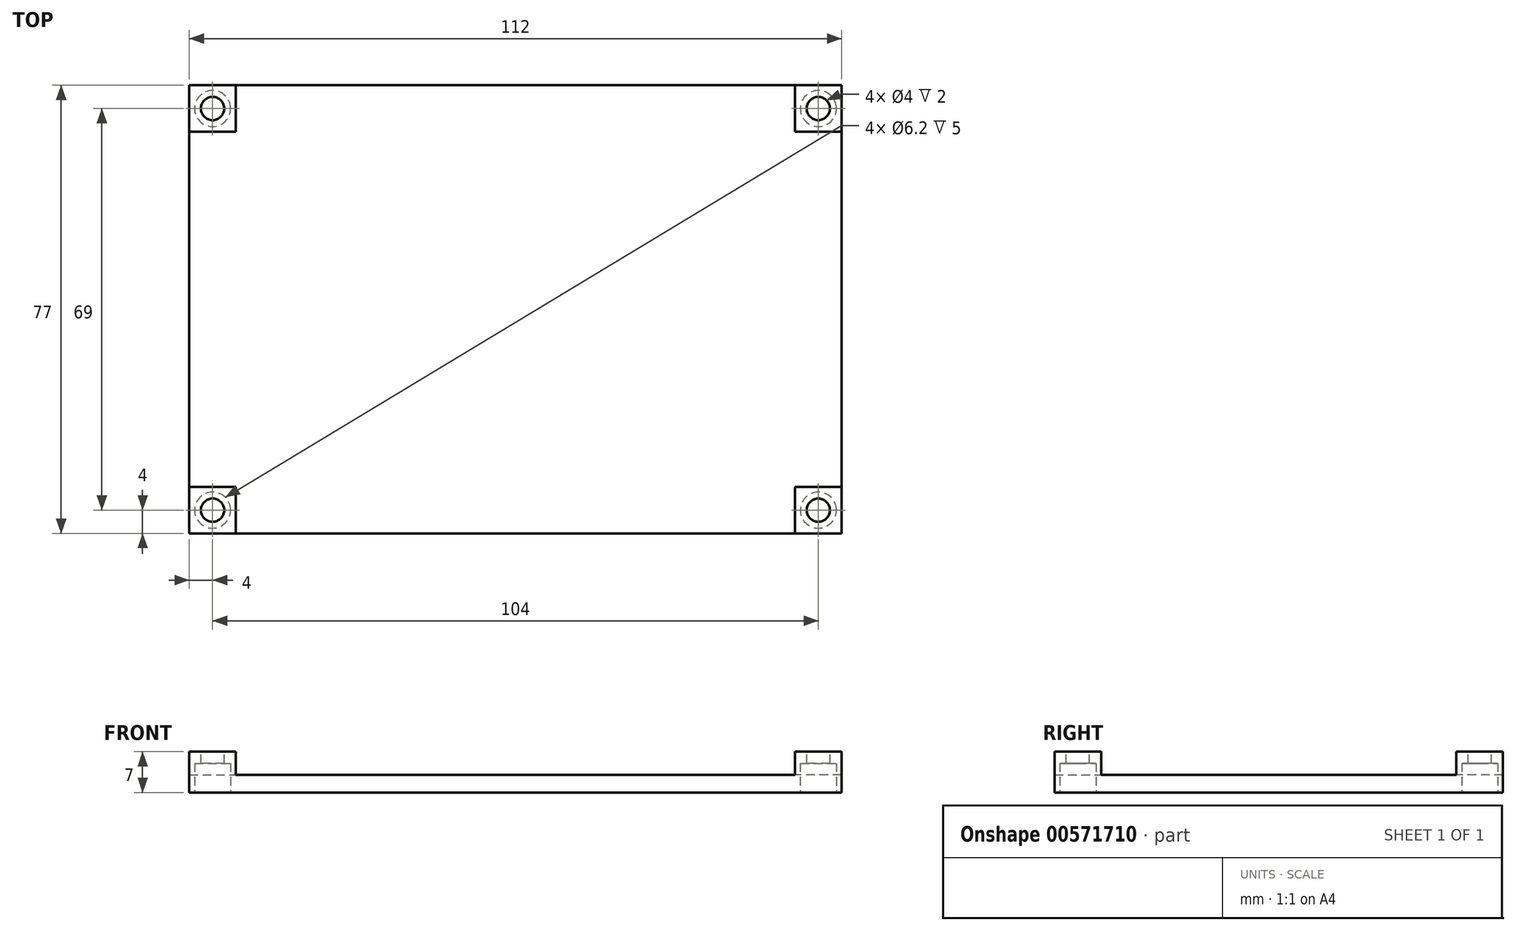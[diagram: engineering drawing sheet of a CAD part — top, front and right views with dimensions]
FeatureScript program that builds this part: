
annotation { "Feature Type Name" : "Feature", "Feature Type Description" : "" }
export const myFeature = defineFeature(function(context is Context, id is Id, definition is map)
    precondition{}
    {
        {
            var Q0;
            Q0=qCreatedBy(makeId("Top.planeOp"),FACE);
            var sketch = newSketch(context, id + "F0", { "sketchPlane" : qUnion([Q0])});
            skLineSegment(sketch, "E0.bottom", {"start": v(56, -38.5) * mm, "end": v(-56, -38.5) * mm});
            skLineSegment(sketch, "E0.top", {"start": v(56, 38.5) * mm, "end": v(-56, 38.5) * mm});
            skLineSegment(sketch, "E0.left", {"start": v(56, -38.5) * mm, "end": v(56, 38.5) * mm});
            skLineSegment(sketch, "E0.right", {"start": v(-56, -38.5) * mm, "end": v(-56, 38.5) * mm});
            skPoint(sketch, "E0.middle", {"position": v(0, 0) * mm});
            skSolve(sketch);
        }
        {
            var Q0;
            Q0=makeQuery(id+"F0.imprint","IMPRINT",FACE,{"disambiguationData":[TD([[makeQuery(id+"F0.imprint","IMPRINT",EDGE,{"derivedFrom":sQuery(id+"F0.wireOp",EDGE,"E0.bottom")}),-1.0]])]});
            extrude(context, id + "F1", {"entities" : qUnion([Q0]), "depth" : 3 * mm, "offsetDistance" : 25.4 * mm});
        }
        {
            var Q0;
            Q0=makeQuery(id+"F1.opExtrude","CAP_FACE",FACE,{"disambiguationData":[OSD([sQuery(id+"F0.wireOp",EDGE,"E0.bottom"),sQuery(id+"F0.wireOp",EDGE,"E0.top"),sQuery(id+"F0.wireOp",EDGE,"E0.left"),sQuery(id+"F0.wireOp",EDGE,"E0.right")])],"isStart":false});
            var sketch = newSketch(context, id + "F2", { "sketchPlane" : qUnion([Q0])});
            skLineSegment(sketch, "E1.bottom", {"start": v(-56, 38.5) * mm, "end": v(-48, 38.5) * mm});
            skLineSegment(sketch, "E1.top", {"start": v(-56, 30.5) * mm, "end": v(-48, 30.5) * mm});
            skLineSegment(sketch, "E1.left", {"start": v(-56, 38.5) * mm, "end": v(-56, 30.5) * mm});
            skLineSegment(sketch, "E1.right", {"start": v(-48, 38.5) * mm, "end": v(-48, 30.5) * mm});
            skLineSegment(sketch, "E2.bottom", {"start": v(56, 38.5) * mm, "end": v(48, 38.5) * mm});
            skLineSegment(sketch, "E2.top", {"start": v(56, 30.5) * mm, "end": v(48, 30.5) * mm});
            skLineSegment(sketch, "E2.left", {"start": v(56, 38.5) * mm, "end": v(56, 30.5) * mm});
            skLineSegment(sketch, "E2.right", {"start": v(48, 38.5) * mm, "end": v(48, 30.5) * mm});
            skLineSegment(sketch, "E3.bottom", {"start": v(56, -38.5) * mm, "end": v(48, -38.5) * mm});
            skLineSegment(sketch, "E3.top", {"start": v(56, -30.5) * mm, "end": v(48, -30.5) * mm});
            skLineSegment(sketch, "E3.left", {"start": v(56, -38.5) * mm, "end": v(56, -30.5) * mm});
            skLineSegment(sketch, "E3.right", {"start": v(48, -38.5) * mm, "end": v(48, -30.5) * mm});
            skLineSegment(sketch, "E4.bottom", {"start": v(-56, -38.5) * mm, "end": v(-48, -38.5) * mm});
            skLineSegment(sketch, "E4.top", {"start": v(-56, -30.5) * mm, "end": v(-48, -30.5) * mm});
            skLineSegment(sketch, "E4.left", {"start": v(-56, -38.5) * mm, "end": v(-56, -30.5) * mm});
            skLineSegment(sketch, "E4.right", {"start": v(-48, -38.5) * mm, "end": v(-48, -30.5) * mm});
            skSolve(sketch);
        }
        {
            var Q0;
            Q0=makeQuery(id+"F2.imprint","IMPRINT",FACE,{"disambiguationData":[TD([[makeQuery(id+"F2.imprint","IMPRINT",EDGE,{"derivedFrom":sQuery(id+"F2.wireOp",EDGE,"E1.bottom")}),1.0]])]});
            var Q1;
            Q1=makeQuery(id+"F2.imprint","IMPRINT",FACE,{"disambiguationData":[TD([[makeQuery(id+"F2.imprint","IMPRINT",EDGE,{"derivedFrom":sQuery(id+"F2.wireOp",EDGE,"E4.bottom")}),-1.0]])]});
            var Q2;
            Q2=makeQuery(id+"F2.imprint","IMPRINT",FACE,{"disambiguationData":[TD([[makeQuery(id+"F2.imprint","IMPRINT",EDGE,{"derivedFrom":sQuery(id+"F2.wireOp",EDGE,"E3.bottom")}),-1.0]])]});
            var Q3;
            Q3=makeQuery(id+"F2.imprint","IMPRINT",FACE,{"disambiguationData":[TD([[makeQuery(id+"F2.imprint","IMPRINT",EDGE,{"derivedFrom":sQuery(id+"F2.wireOp",EDGE,"E2.bottom")}),1.0]])]});
            extrude(context, id + "F3", {"entities" : qUnion([Q0, Q1, Q2, Q3]), "operationType" : NewBodyOperationType.ADD, "depth" : 4 * mm, "offsetDistance" : 25.4 * mm});
        }
        {
            var Q0;
            Q0=makeQuery(id+"F3.opExtrude","CAP_FACE",FACE,{"disambiguationData":[OSD([sQuery(id+"F2.wireOp",EDGE,"E1.bottom"),sQuery(id+"F2.wireOp",EDGE,"E1.top"),sQuery(id+"F2.wireOp",EDGE,"E1.left"),sQuery(id+"F2.wireOp",EDGE,"E1.right")])],"isStart":false});
            var sketch = newSketch(context, id + "F4", { "sketchPlane" : qUnion([Q0])});
            skCircle(sketch, "E5", {"center": v(-52, 34.5) * mm, "radius": 2 * mm});
            skCircle(sketch, "E6", {"center": v(52, 34.5) * mm, "radius": 2 * mm});
            skCircle(sketch, "E7", {"center": v(-52, -34.5) * mm, "radius": 2 * mm});
            skCircle(sketch, "E8", {"center": v(52, -34.5) * mm, "radius": 2 * mm});
            skSolve(sketch);
        }
        {
            var Q0;
            Q0 = qSketchRegion(id + "F4", true);
            extrude(context, id + "F5", {"entities" : qUnion([Q0]), "operationType" : NewBodyOperationType.REMOVE, "oppositeDirection" : true, "depth" : 25.4 * mm, "offsetDistance" : 25.4 * mm});
        }
        {
            var Q0;
            Q0=makeQuery(id+"F1.opExtrude","CAP_FACE",FACE,{"disambiguationData":[OSD([sQuery(id+"F0.wireOp",EDGE,"E0.bottom"),sQuery(id+"F0.wireOp",EDGE,"E0.top"),sQuery(id+"F0.wireOp",EDGE,"E0.left"),sQuery(id+"F0.wireOp",EDGE,"E0.right")])],"isStart":true});
            var sketch = newSketch(context, id + "F6", { "sketchPlane" : qUnion([Q0])});
            skCircle(sketch, "E9", {"center": v(-52, 34.5) * mm, "radius": 3.1 * mm});
            skCircle(sketch, "E10", {"center": v(-52, -34.5) * mm, "radius": 3.1 * mm});
            skCircle(sketch, "E11", {"center": v(52, 34.5) * mm, "radius": 3.1 * mm});
            skCircle(sketch, "E12", {"center": v(52, -34.5) * mm, "radius": 3.1 * mm});
            skSolve(sketch);
        }
        {
            var Q0;
            Q0=makeQuery(id+"F6.imprint","IMPRINT",FACE,{"disambiguationData":[TD([[makeQuery(id+"F6.imprint","IMPRINT",EDGE,{"derivedFrom":sQuery(id+"F6.wireOp",EDGE,"E9")}),1.0]])]});
            var Q1;
            Q1=makeQuery(id+"F6.imprint","IMPRINT",FACE,{"disambiguationData":[TD([[makeQuery(id+"F6.imprint","IMPRINT",EDGE,{"derivedFrom":sQuery(id+"F6.wireOp",EDGE,"E11")}),1.0]])]});
            var Q2;
            Q2=makeQuery(id+"F6.imprint","IMPRINT",FACE,{"disambiguationData":[TD([[makeQuery(id+"F6.imprint","IMPRINT",EDGE,{"derivedFrom":sQuery(id+"F6.wireOp",EDGE,"E12")}),1.0]])]});
            var Q3;
            Q3=makeQuery(id+"F6.imprint","IMPRINT",FACE,{"disambiguationData":[TD([[makeQuery(id+"F6.imprint","IMPRINT",EDGE,{"derivedFrom":sQuery(id+"F6.wireOp",EDGE,"E10")}),1.0]])]});
            extrude(context, id + "F7", {"entities" : qUnion([Q0, Q1, Q2, Q3]), "operationType" : NewBodyOperationType.REMOVE, "oppositeDirection" : true, "depth" : 5 * mm, "offsetDistance" : 25.4 * mm});
        }
    });
